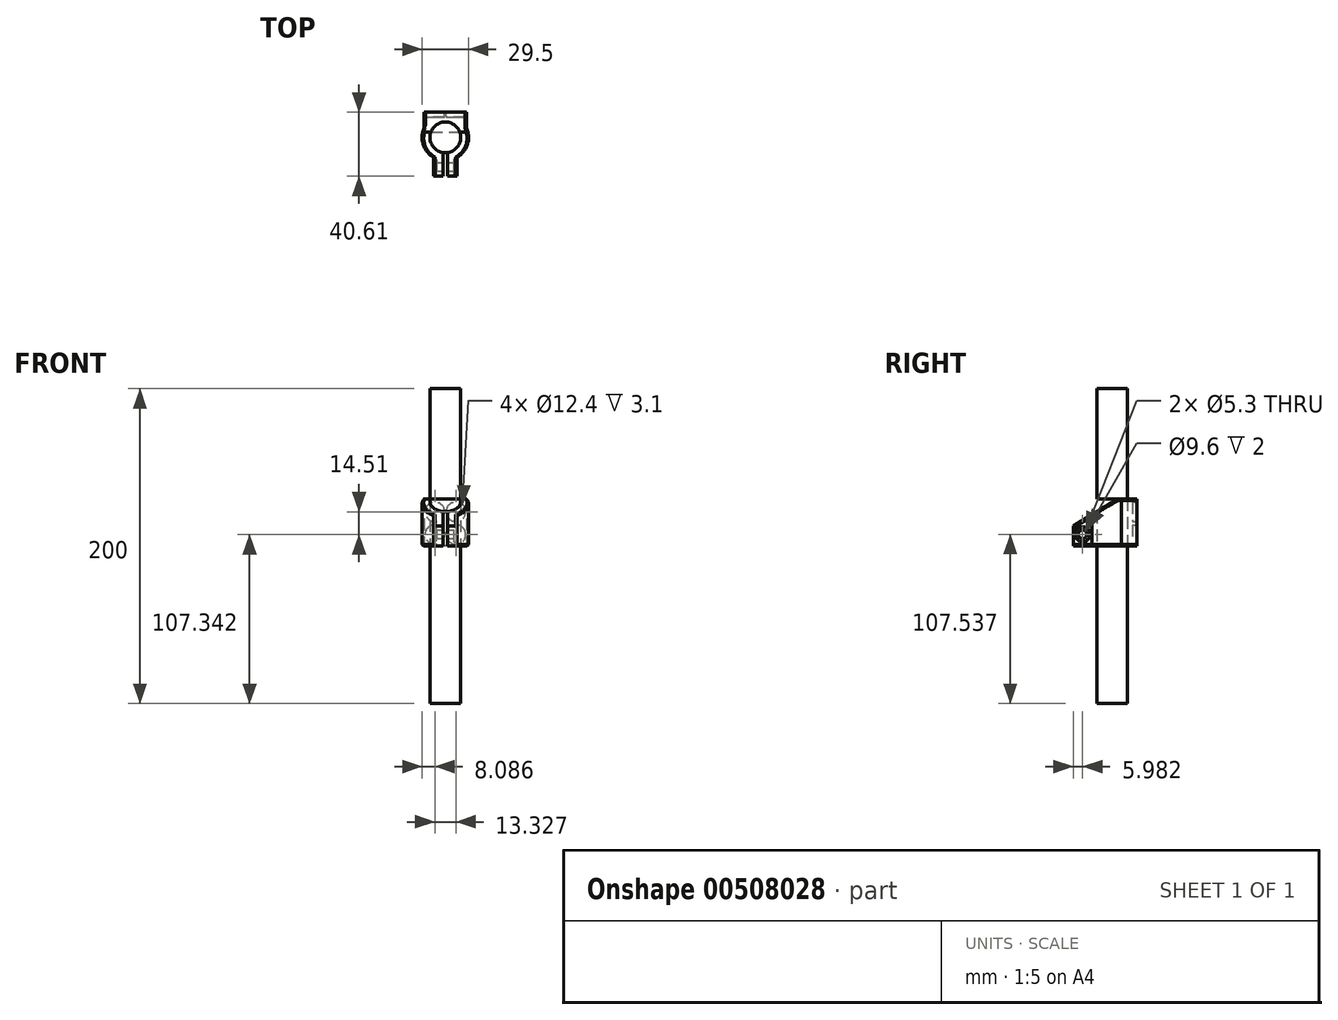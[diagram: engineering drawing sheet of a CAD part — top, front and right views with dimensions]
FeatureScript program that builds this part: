
annotation { "Feature Type Name" : "Feature", "Feature Type Description" : "" }
export const myFeature = defineFeature(function(context is Context, id is Id, definition is map)
    precondition{}
    {
        {
            var Q0;
            Q0=qCreatedBy(makeId("Top.planeOp"),FACE);
            var sketch = newSketch(context, id + "F0", { "sketchPlane" : qUnion([Q0])});
            skCircle(sketch, "E0", {"center": v(0, 0) * mm, "radius": 9.75 * mm});
            skSolve(sketch);
        }
        {
            var Q0;
            Q0 = qSketchRegion(id + "F0", true);
            extrude(context, id + "F1", {"entities" : qUnion([Q0]), "endBound" : BoundingType.SYMMETRIC, "depth" : 200 * mm});
        }
        {
            var Q0;
            Q0=qCreatedBy(makeId("Top.planeOp"),FACE);
            var sketch = newSketch(context, id + "F2", { "sketchPlane" : qUnion([Q0])});
            skCircle(sketch, "E1.0", {"center": v(0, 0) * mm, "radius": 9.75 * mm});
            skCircle(sketch, "E2", {"center": v(0, 0) * mm, "radius": 14.75 * mm});
            skLineSegment(sketch, "E3", {"start": v(0, 19.34) * mm, "end": v(0, -20.79) * mm, "construction": true});
            skLineSegment(sketch, "E4", {"start": v(-1.5, -24.67) * mm, "end": v(-7.5, -24.67) * mm});
            skLineSegment(sketch, "E5", {"start": v(-7.5, -24.67) * mm, "end": v(-7.5, -12.7) * mm});
            skLineSegment(sketch, "E6", {"start": v(1.5, -24.67) * mm, "end": v(7.5, -24.67) * mm});
            skLineSegment(sketch, "E7", {"start": v(7.5, -24.67) * mm, "end": v(7.5, -12.7) * mm});
            skLineSegment(sketch, "E8.trimOffspring", {"start": v(1.5, -9.63) * mm, "end": v(1.5, -24.67) * mm});
            skLineSegment(sketch, "E9.trimOffspring", {"start": v(-1.5, -9.63) * mm, "end": v(-1.5, -24.67) * mm});
            skLineSegment(sketch, "E10", {"start": v(-13.5, 5.94) * mm, "end": v(-13.5, 15.94) * mm});
            skLineSegment(sketch, "E11", {"start": v(13.5, 15.94) * mm, "end": v(13.5, 5.94) * mm});
            skLineSegment(sketch, "E12", {"start": v(13.5, 15.94) * mm, "end": v(-13.5, 15.94) * mm});
            skSolve(sketch);
        }
        {
            var Q0;
            {var subQ0=sQuery(id+"F2.wireOp",EDGE,"E10");Q0=makeQuery(id+"F2.imprint","IMPRINT",FACE,{"disambiguationData":[TD([[makeQuery(id+"F2.imprint","IMPRINT",EDGE,{"derivedFrom":subQ0}),-1.0]])]});}
            var Q1;
            {var subQ4=sQuery(id+"F2.wireOp",EDGE,"E4");Q1=makeQuery(id+"F2.imprint","IMPRINT",FACE,{"disambiguationData":[TD([[makeQuery(id+"F2.imprint","IMPRINT",EDGE,{"derivedFrom":subQ4}),-1.0]])]});}
            var Q2;
            {var subQ4=sQuery(id+"F2.wireOp",EDGE,"E6");Q2=makeQuery(id+"F2.imprint","IMPRINT",FACE,{"disambiguationData":[TD([[makeQuery(id+"F2.imprint","IMPRINT",EDGE,{"derivedFrom":subQ4}),1.0]])]});}
            var Q3;
            {var subQ5=sQuery(id+"F2.wireOp",EDGE,"E1.0");var subQ8=sQuery(id+"F2.wireOp",EDGE,"E8.trimOffspring");var subQ9=makeQuery(id+"F2.imprint","INTERSECT",VERTEX,{"derivedFrom":[subQ5,subQ8]});Q3=makeQuery(id+"F2.imprint","IMPRINT",FACE,{"disambiguationData":[TD([[makeQuery(id+"F2.imprint","IMPRINT",EDGE,{"disambiguationData":[TD([[subQ9,-1.0]])],"derivedFrom":subQ5}),-1.0]])]});}
            extrude(context, id + "F3", {"entities" : qUnion([Q0, Q1, Q2, Q3]), "depth" : 30 * mm});
        }
        {
            var Q0;
            Q0=makeQuery(id+"F3.opExtrude","SWEPT_FACE",FACE,{"disambiguationData":[OSD([sQuery(id+"F2.wireOp",EDGE,"E12")])]});
            var sketch = newSketch(context, id + "F4", { "sketchPlane" : qUnion([Q0])});
            skLineSegment(sketch, "E13", {"start": v(0, 30) * mm, "end": v(0, 0) * mm, "construction": true});
            skCircle(sketch, "E14", {"center": v(6.66, 21.85) * mm, "radius": 6.2 * mm});
            skCircle(sketch, "E15", {"center": v(6.66, 7.34) * mm, "radius": 6.2 * mm});
            skCircle(sketch, "E16.MirrorC", {"center": v(-6.66, 21.85) * mm, "radius": 6.2 * mm});
            skCircle(sketch, "E17.MirrorC", {"center": v(-6.66, 7.34) * mm, "radius": 6.2 * mm});
            skSolve(sketch);
        }
        {
            var Q0;
            Q0 = qSketchRegion(id + "F4", true);
            extrude(context, id + "F5", {"entities" : qUnion([Q0]), "operationType" : NewBodyOperationType.REMOVE, "oppositeDirection" : true, "depth" : 3.1 * mm});
        }
        {
            var Q0;
            Q0=makeQuery(id+"F3.opExtrude","SWEPT_FACE",FACE,{"disambiguationData":[OSD([sQuery(id+"F2.wireOp",EDGE,"E11")])]});
            var sketch = newSketch(context, id + "F6", { "sketchPlane" : qUnion([Q0])});
            skLineSegment(sketch, "E18", {"start": v(3.49, 30) * mm, "end": v(-24.67, 12.9) * mm});
            skLineSegment(sketch, "E19", {"start": v(3.49, 30) * mm, "end": v(-24.67, 30) * mm});
            skLineSegment(sketch, "E20", {"start": v(-24.67, 30) * mm, "end": v(-24.67, 12.9) * mm});
            skSolve(sketch);
        }
        {
            var Q0;
            Q0 = qSketchRegion(id + "F6", true);
            extrude(context, id + "F7", {"entities" : qUnion([Q0]), "operationType" : NewBodyOperationType.REMOVE, "endBound" : BoundingType.SYMMETRIC, "oppositeDirection" : true, "depth" : 100 * mm});
        }
        {
            var Q0;
            Q0=makeQuery(id+"F3.opExtrude","SWEPT_FACE",FACE,{"disambiguationData":[OSD([sQuery(id+"F2.wireOp",EDGE,"E7")])]});
            var sketch = newSketch(context, id + "F8", { "sketchPlane" : qUnion([Q0])});
            skCircle(sketch, "E21", {"center": v(-18.69, 7.54) * mm, "radius": 2.65 * mm});
            skCircle(sketch, "E22", {"center": v(-18.69, 7.54) * mm, "radius": 4.8 * mm});
            skLineSegment(sketch, "E23", {"start": v(-18.69, 0) * mm, "end": v(-18.69, 16.53) * mm, "construction": true});
            skSolve(sketch);
        }
        {
            var Q0;
            Q0=makeQuery(id+"F8.imprint","IMPRINT",FACE,{"disambiguationData":[TD([[makeQuery(id+"F8.imprint","IMPRINT",EDGE,{"derivedFrom":sQuery(id+"F8.wireOp",EDGE,"E21")}),1.0]])]});
            extrude(context, id + "F9", {"entities" : qUnion([Q0]), "operationType" : NewBodyOperationType.REMOVE, "oppositeDirection" : true, "depth" : 25 * mm});
        }
        {
            var Q0;
            Q0=makeQuery(id+"F8.imprint","IMPRINT",FACE,{"disambiguationData":[TD([[makeQuery(id+"F8.imprint","IMPRINT",EDGE,{"derivedFrom":sQuery(id+"F8.wireOp",EDGE,"E21")}),-1.0]])]});
            extrude(context, id + "F10", {"entities" : qUnion([Q0]), "operationType" : NewBodyOperationType.REMOVE, "oppositeDirection" : true, "depth" : 2 * mm});
        }
        {
            var Q0;
            Q0=makeQuery(id+"F3.opExtrude","SWEPT_FACE",FACE,{"disambiguationData":[OSD([sQuery(id+"F2.wireOp",EDGE,"E5")])]});
            var sketch = newSketch(context, id + "F11", { "sketchPlane" : qUnion([Q0])});
            skCircle(sketch, "E24.cCircle", {"center": v(18.69, 7.54) * mm, "radius": 4.1 * mm, "construction": true});
            skLineSegment(sketch, "E24.0", {"start": v(16.32, 11.64) * mm, "end": v(21.05, 11.64) * mm});
            skLineSegment(sketch, "E24.1", {"start": v(21.05, 11.64) * mm, "end": v(23.42, 7.54) * mm});
            skLineSegment(sketch, "E24.2", {"start": v(23.42, 7.54) * mm, "end": v(21.05, 3.44) * mm});
            skLineSegment(sketch, "E24.3", {"start": v(21.05, 3.44) * mm, "end": v(16.32, 3.44) * mm});
            skLineSegment(sketch, "E24.4", {"start": v(16.32, 3.44) * mm, "end": v(13.95, 7.54) * mm});
            skLineSegment(sketch, "E24.5", {"start": v(13.95, 7.54) * mm, "end": v(16.32, 11.64) * mm});
            skPoint(sketch, "E24.0.midPoint", {"position": v(18.69, 11.64) * mm});
            skSolve(sketch);
        }
        {
            var Q0;
            Q0 = qSketchRegion(id + "F11", true);
            extrude(context, id + "F12", {"entities" : qUnion([Q0]), "operationType" : NewBodyOperationType.REMOVE, "oppositeDirection" : true, "depth" : 2 * mm});
        }
        {
            var Q0;
            Q0=makeQuery(id+"F3.opExtrude","CAP_EDGE",EDGE,{"disambiguationData":[OSD([sQuery(id+"F2.wireOp",EDGE,"E11")])],"isStart":false});
            var Q1;
            {var subQ0=sQuery(id+"F2.wireOp",EDGE,"E2");Q1=makeQuery(id+"F3.opExtrude","CAP_EDGE",EDGE,{"disambiguationData":[OSD([subQ0]),TDD([makeQuery(id+"F2.imprint","IMPRINT",EDGE,{"disambiguationData":[TD([[makeQuery(id+"F2.imprint","INTERSECT",VERTEX,{"derivedFrom":[subQ0,sQuery(id+"F2.wireOp",EDGE,"E7")]}),-1.0]])],"derivedFrom":subQ0})])],"isStart":false});}
            var Q2;
            {var subQ0=sQuery(id+"F2.wireOp",EDGE,"E2");Q2=makeQuery(id+"F7.boolean.opBoolean","INTERSECT",EDGE,{"derivedFrom":[makeQuery(id+"F3.opExtrude","SWEPT_FACE",FACE,{"disambiguationData":[OSD([subQ0]),TDD([makeQuery(id+"F2.imprint","IMPRINT",EDGE,{"disambiguationData":[TD([[makeQuery(id+"F2.imprint","INTERSECT",VERTEX,{"derivedFrom":[subQ0,sQuery(id+"F2.wireOp",EDGE,"E7")]}),-1.0]])],"derivedFrom":subQ0})])]}),makeQuery(id+"F7.opExtrude","SWEPT_FACE",FACE,{"disambiguationData":[OSD([sQuery(id+"F6.wireOp",EDGE,"E18")])]})]});}
            var Q3;
            Q3=makeQuery(id+"F7.boolean.opBoolean","INTERSECT",EDGE,{"derivedFrom":[makeQuery(id+"F3.opExtrude","SWEPT_FACE",FACE,{"disambiguationData":[OSD([sQuery(id+"F2.wireOp",EDGE,"E7")])]}),makeQuery(id+"F7.opExtrude","SWEPT_FACE",FACE,{"disambiguationData":[OSD([sQuery(id+"F6.wireOp",EDGE,"E18")])]})]});
            var Q4;
            Q4=makeQuery(id+"F7.boolean.opBoolean","INTERSECT",EDGE,{"derivedFrom":[makeQuery(id+"F3.opExtrude","SWEPT_FACE",FACE,{"disambiguationData":[OSD([sQuery(id+"F2.wireOp",EDGE,"E5")])]}),makeQuery(id+"F7.opExtrude","SWEPT_FACE",FACE,{"disambiguationData":[OSD([sQuery(id+"F6.wireOp",EDGE,"E18")])]})]});
            var Q5;
            {var subQ0=sQuery(id+"F2.wireOp",EDGE,"E2");Q5=makeQuery(id+"F7.boolean.opBoolean","INTERSECT",EDGE,{"derivedFrom":[makeQuery(id+"F3.opExtrude","SWEPT_FACE",FACE,{"disambiguationData":[OSD([subQ0]),TDD([makeQuery(id+"F2.imprint","IMPRINT",EDGE,{"disambiguationData":[TD([[makeQuery(id+"F2.imprint","INTERSECT",VERTEX,{"derivedFrom":[subQ0,sQuery(id+"F2.wireOp",EDGE,"E5")]}),1.0]])],"derivedFrom":subQ0})])]}),makeQuery(id+"F7.opExtrude","SWEPT_FACE",FACE,{"disambiguationData":[OSD([sQuery(id+"F6.wireOp",EDGE,"E18")])]})]});}
            var Q6;
            Q6=makeQuery(id+"F3.opExtrude","CAP_EDGE",EDGE,{"disambiguationData":[OSD([sQuery(id+"F2.wireOp",EDGE,"E10")])],"isStart":false});
            var Q7;
            Q7=makeQuery(id+"F3.opExtrude","CAP_EDGE",EDGE,{"disambiguationData":[OSD([sQuery(id+"F2.wireOp",EDGE,"E10")])],"isStart":true});
            var Q8;
            {var subQ0=sQuery(id+"F2.wireOp",EDGE,"E2");Q8=makeQuery(id+"F3.opExtrude","CAP_EDGE",EDGE,{"disambiguationData":[OSD([subQ0]),TDD([makeQuery(id+"F2.imprint","IMPRINT",EDGE,{"disambiguationData":[TD([[makeQuery(id+"F2.imprint","INTERSECT",VERTEX,{"derivedFrom":[subQ0,sQuery(id+"F2.wireOp",EDGE,"E5")]}),1.0]])],"derivedFrom":subQ0})])],"isStart":true});}
            var Q9;
            Q9=makeQuery(id+"F3.opExtrude","CAP_EDGE",EDGE,{"disambiguationData":[OSD([sQuery(id+"F2.wireOp",EDGE,"E5")])],"isStart":true});
            var Q10;
            Q10=makeQuery(id+"F3.opExtrude","CAP_EDGE",EDGE,{"disambiguationData":[OSD([sQuery(id+"F2.wireOp",EDGE,"E7")])],"isStart":true});
            var Q11;
            {var subQ0=sQuery(id+"F2.wireOp",EDGE,"E2");Q11=makeQuery(id+"F3.opExtrude","CAP_EDGE",EDGE,{"disambiguationData":[OSD([subQ0]),TDD([makeQuery(id+"F2.imprint","IMPRINT",EDGE,{"disambiguationData":[TD([[makeQuery(id+"F2.imprint","INTERSECT",VERTEX,{"derivedFrom":[subQ0,sQuery(id+"F2.wireOp",EDGE,"E7")]}),-1.0]])],"derivedFrom":subQ0})])],"isStart":true});}
            var Q12;
            Q12=makeQuery(id+"F3.opExtrude","CAP_EDGE",EDGE,{"disambiguationData":[OSD([sQuery(id+"F2.wireOp",EDGE,"E11")])],"isStart":true});
            chamfer(context, id + "F13", {"entities" : qUnion([Q0, Q1, Q2, Q3, Q4, Q5, Q6, Q7, Q8, Q9, Q10, Q11, Q12]), "width" : 1 * mm, "tangentPropagation" : true});
        }
    });
